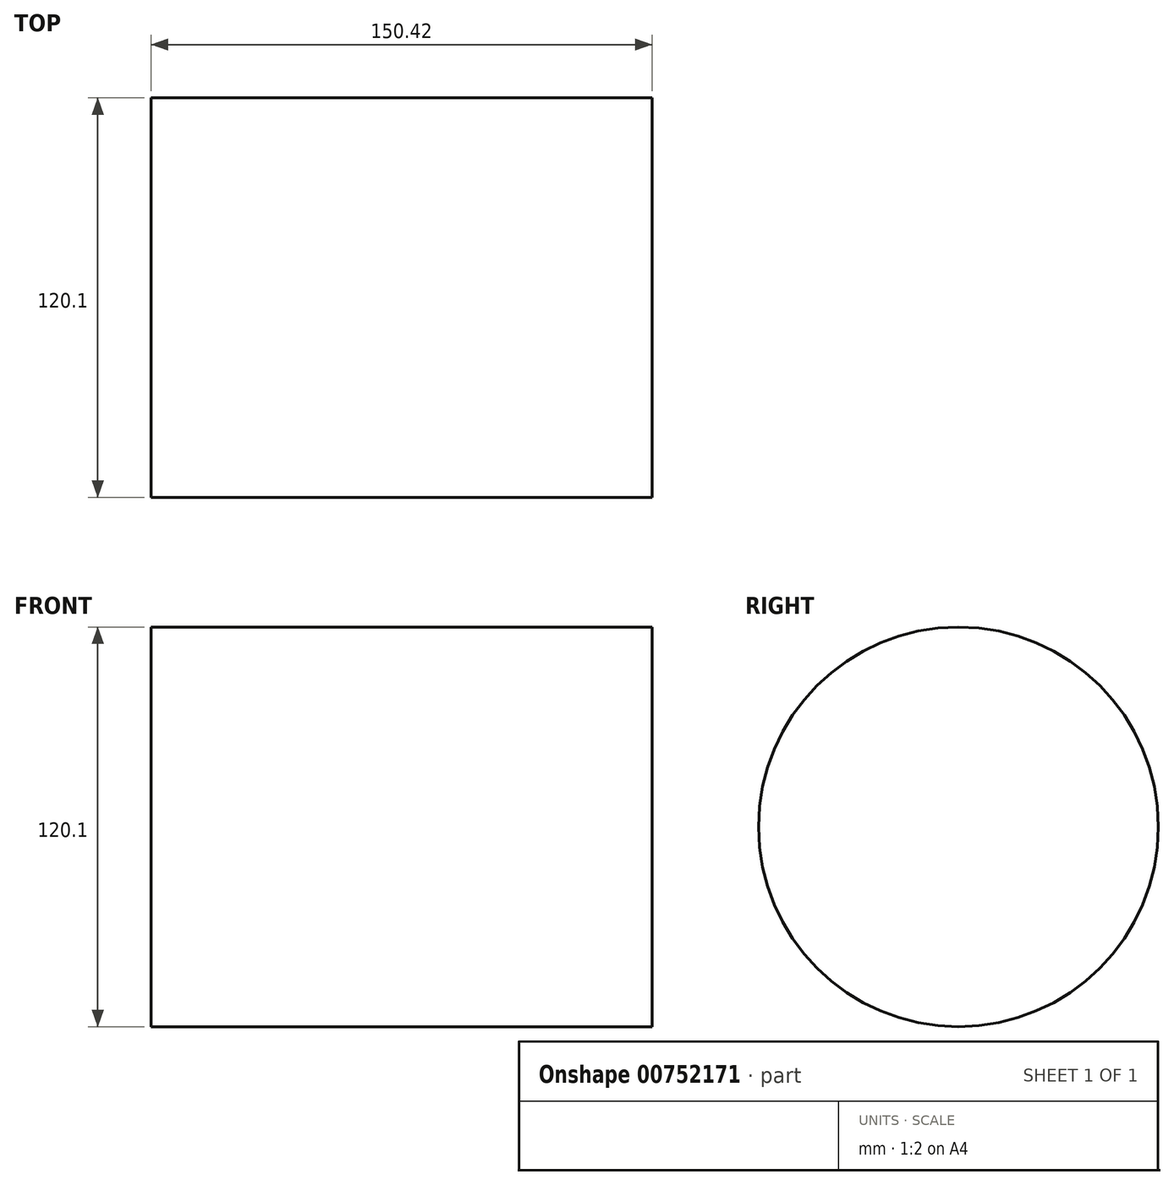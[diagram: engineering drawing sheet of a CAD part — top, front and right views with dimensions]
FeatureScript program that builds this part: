
annotation { "Feature Type Name" : "Feature", "Feature Type Description" : "" }
export const myFeature = defineFeature(function(context is Context, id is Id, definition is map)
    precondition{}
    {
        {
            var Q0;
            Q0=qCreatedBy(makeId("Front.planeOp"),FACE);
            var sketch = newSketch(context, id + "F0", { "sketchPlane" : qUnion([Q0])});
            skLineSegment(sketch, "E0.bottom", {"start": v(-74.93, 26.77) * mm, "end": v(75.5, 26.77) * mm});
            skLineSegment(sketch, "E0.top", {"start": v(-74.93, -33.28) * mm, "end": v(75.5, -33.28) * mm});
            skLineSegment(sketch, "E0.left", {"start": v(-74.93, 26.77) * mm, "end": v(-74.93, -33.28) * mm});
            skLineSegment(sketch, "E0.right", {"start": v(75.5, 26.77) * mm, "end": v(75.5, -33.28) * mm});
            skSolve(sketch);
        }
        {
            var Q0;
            Q0=makeQuery(id+"F0.imprint","IMPRINT",FACE,{"disambiguationData":[TD([[makeQuery(id+"F0.imprint","IMPRINT",EDGE,{"derivedFrom":sQuery(id+"F0.wireOp",EDGE,"E0.bottom")}),-1.0]])]});
            var Q1;
            Q1=sQuery(id+"F0.wireOp",EDGE,"E0.bottom");
            revolve(context, id + "F1", {"surfaceOperationType" : NewSurfaceOperationType.NEW, "entities" : qUnion([Q0]), "axis" : qUnion([Q1]), "revolveType" : RevolveType.FULL});
        }
    });
